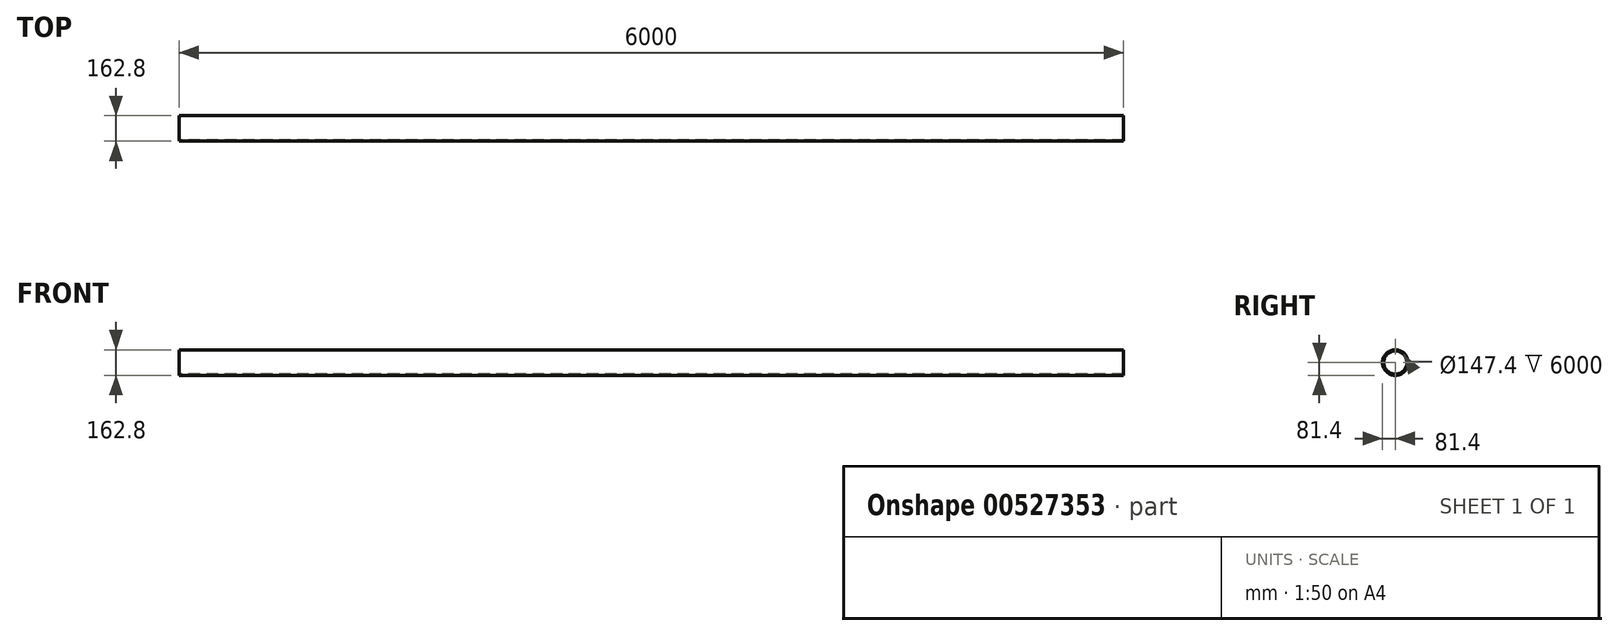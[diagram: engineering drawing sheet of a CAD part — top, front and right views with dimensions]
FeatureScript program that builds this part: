
annotation { "Feature Type Name" : "Feature", "Feature Type Description" : "" }
export const myFeature = defineFeature(function(context is Context, id is Id, definition is map)
    precondition{}
    {
        {
            var Q0;
            Q0=qCreatedBy(makeId("Right.planeOp"),FACE);
            var sketch = newSketch(context, id + "F0", { "sketchPlane" : qUnion([Q0])});
            skCircle(sketch, "E0", {"center": v(0, 0) * mm, "radius": 81.4 * mm});
            skCircle(sketch, "E1.0", {"center": v(0, 0) * mm, "radius": 73.7 * mm});
            skSolve(sketch);
        }
        {
            var Q0;
            Q0=makeQuery(id+"F0.imprint","IMPRINT",FACE,{"disambiguationData":[TD([[makeQuery(id+"F0.imprint","IMPRINT",EDGE,{"derivedFrom":sQuery(id+"F0.wireOp",EDGE,"E0")}),1.0]])]});
            extrude(context, id + "F1", {"entities" : qUnion([Q0]), "depth" : 6000 * mm, "offsetDistance" : 25 * mm});
        }
    });
